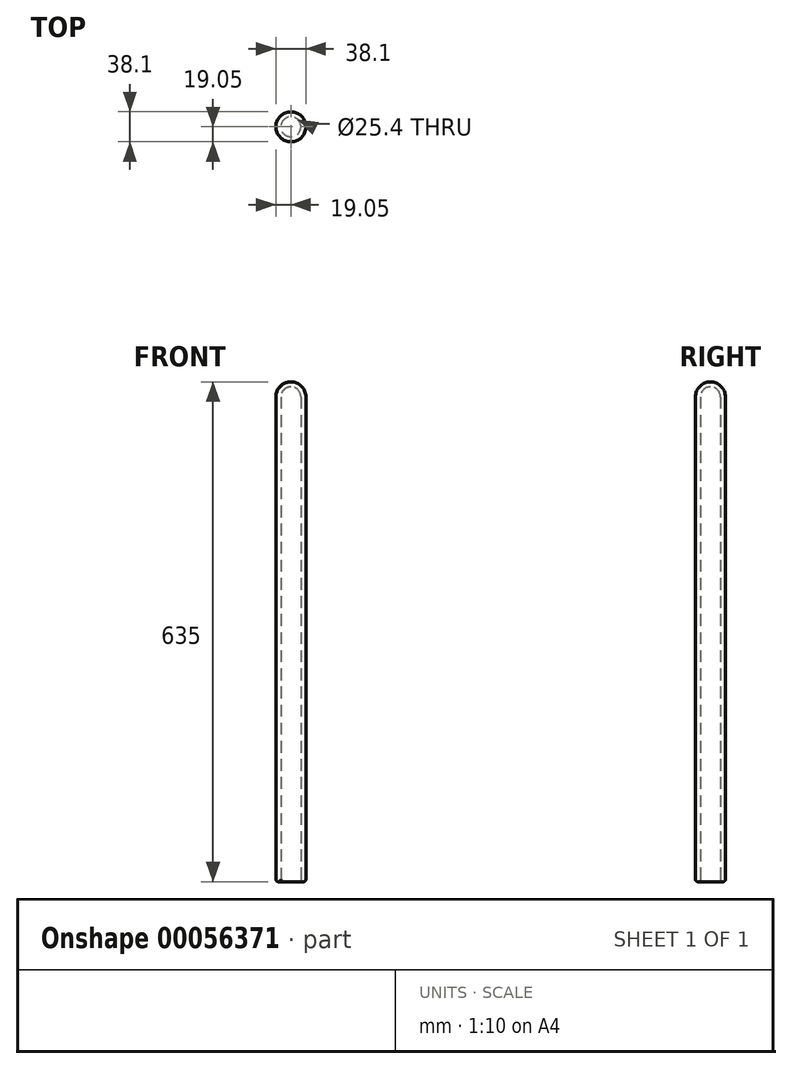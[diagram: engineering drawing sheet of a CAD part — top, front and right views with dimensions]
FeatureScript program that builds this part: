
annotation { "Feature Type Name" : "Feature", "Feature Type Description" : "" }
export const myFeature = defineFeature(function(context is Context, id is Id, definition is map)
    precondition{}
    {
        {
            var Q0;
            Q0=qCreatedBy(makeId("Right.planeOp"),FACE);
            var sketch = newSketch(context, id + "F0", { "sketchPlane" : qUnion([Q0])});
            skLineSegment(sketch, "E0.rect.bottom", {"start": v(19.05, -317.5) * mm, "end": v(-19.05, -317.5) * mm});
            skLineSegment(sketch, "E0.rect.top", {"start": v(19.05, 317.5) * mm, "end": v(-19.05, 317.5) * mm});
            skLineSegment(sketch, "E0.rect.left", {"start": v(19.05, -317.5) * mm, "end": v(19.05, 317.5) * mm});
            skLineSegment(sketch, "E0.rect.right", {"start": v(-19.05, -317.5) * mm, "end": v(-19.05, 317.5) * mm});
            skPoint(sketch, "E0.rect.middle", {"position": v(0, 0) * mm});
            skSolve(sketch);
        }
        {
            var Q0;
            Q0=makeQuery(id+"F0.imprint","IMPRINT",FACE,{"disambiguationData":[TD([[makeQuery(id+"F0.imprint","IMPRINT",EDGE,{"derivedFrom":sQuery(id+"F0.wireOp",EDGE,"E0.rect.bottom")}),-1.0]])]});
            extrude(context, id + "F1", {"entities" : qUnion([Q0]), "depth" : 38.1 * mm});
        }
        {
            var Q0;
            Q0=makeQuery(id+"F1.opExtrude","CAP_EDGE",EDGE,{"disambiguationData":[OSD([sQuery(id+"F0.wireOp",EDGE,"E0.rect.right")])],"isStart":false});
            var Q1;
            Q1=makeQuery(id+"F1.opExtrude","CAP_EDGE",EDGE,{"disambiguationData":[OSD([sQuery(id+"F0.wireOp",EDGE,"E0.rect.right")])],"isStart":true});
            var Q2;
            Q2=makeQuery(id+"F1.opExtrude","CAP_EDGE",EDGE,{"disambiguationData":[OSD([sQuery(id+"F0.wireOp",EDGE,"E0.rect.left")])],"isStart":true});
            var Q3;
            Q3=makeQuery(id+"F1.opExtrude","CAP_EDGE",EDGE,{"disambiguationData":[OSD([sQuery(id+"F0.wireOp",EDGE,"E0.rect.left")])],"isStart":false});
            fillet(context, id + "F2", {"entities" : qUnion([Q0, Q1, Q2, Q3]), "radius" : 19.05 * mm, "tangentPropagation" : true, "allowEdgeOverflow" : false});
        }
        {
            var Q0;
            Q0=makeQuery(id+"F1.opExtrude","SWEPT_FACE",FACE,{"disambiguationData":[OSD([sQuery(id+"F0.wireOp",EDGE,"E0.rect.top")])]});
            fillet(context, id + "F3", {"entities" : qUnion([Q0]), "radius" : 19.05 * mm, "tangentPropagation" : true, "allowEdgeOverflow" : false});
        }
        {
            var Q0;
            Q0=makeQuery(id+"F1.opExtrude","SWEPT_FACE",FACE,{"disambiguationData":[OSD([sQuery(id+"F0.wireOp",EDGE,"E0.rect.bottom")])]});
            shell(context, id + "F4", {"entities" : qUnion([Q0]), "thickness" : 6.35 * mm});
        }
        {
            var Q0;
            Q0=makeQuery(id+"F1.opExtrude","SWEPT_FACE",FACE,{"disambiguationData":[OSD([sQuery(id+"F0.wireOp",EDGE,"E0.rect.bottom")])]});
            fillet(context, id + "F5", {"entities" : qUnion([Q0]), "radius" : 3.17 * mm, "tangentPropagation" : true, "allowEdgeOverflow" : false});
        }
    });
